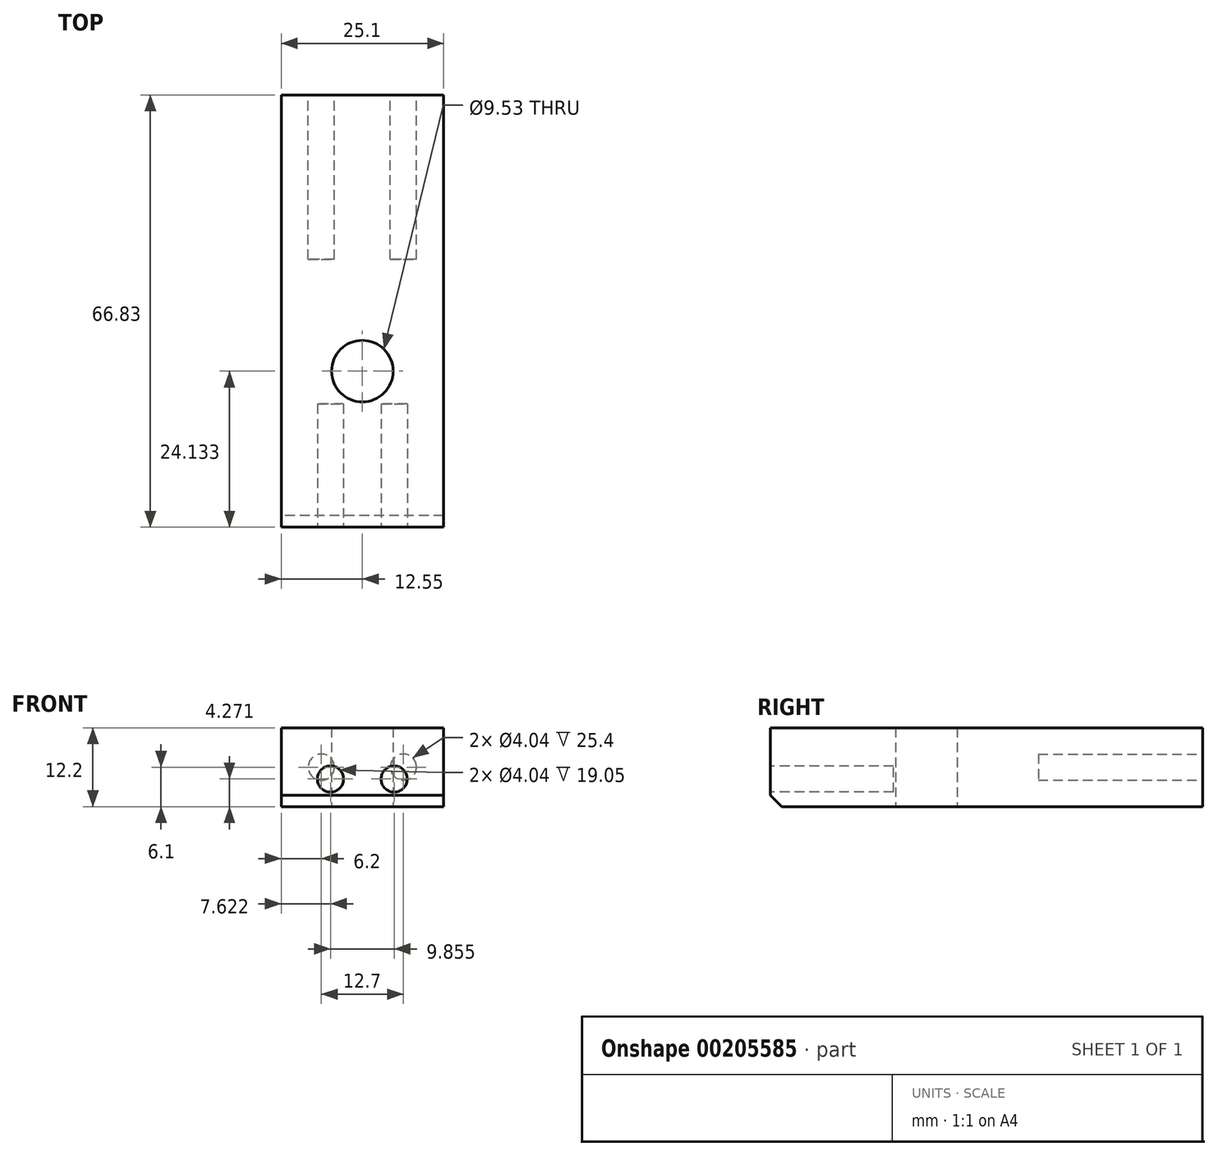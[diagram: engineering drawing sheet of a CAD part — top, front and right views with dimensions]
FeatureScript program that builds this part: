
annotation { "Feature Type Name" : "Feature", "Feature Type Description" : "" }
export const myFeature = defineFeature(function(context is Context, id is Id, definition is map)
    precondition{}
    {
        {
            var Q0;
            Q0=qCreatedBy(makeId("Front.planeOp"),FACE);
            var sketch = newSketch(context, id + "F0", { "sketchPlane" : qUnion([Q0])});
            skLineSegment(sketch, "E0.bottom", {"start": v(-12.55, 6.1) * mm, "end": v(12.55, 6.1) * mm});
            skLineSegment(sketch, "E0.top", {"start": v(-12.55, -6.1) * mm, "end": v(12.55, -6.1) * mm});
            skLineSegment(sketch, "E0.left", {"start": v(-12.55, 6.1) * mm, "end": v(-12.55, -6.1) * mm});
            skLineSegment(sketch, "E0.right", {"start": v(12.55, 6.1) * mm, "end": v(12.55, -6.1) * mm});
            skPoint(sketch, "E0.middle", {"position": v(0, 0) * mm});
            skSolve(sketch);
        }
        {
            var Q0;
            Q0=qSketchRegion(id+"F0",true);
            extrude(context, id + "F1", {"entities" : qUnion([Q0]), "depth" : 66.83 * mm});
        }
        {
            var Q0;
            Q0=makeQuery(id+"F1.opExtrude","CAP_FACE",FACE,{"disambiguationData":[OSD([sQuery(id+"F0.wireOp",EDGE,"E0.bottom"),sQuery(id+"F0.wireOp",EDGE,"E0.top"),sQuery(id+"F0.wireOp",EDGE,"E0.left"),sQuery(id+"F0.wireOp",EDGE,"E0.right")])],"isStart":true});
            var sketch = newSketch(context, id + "F2", { "sketchPlane" : qUnion([Q0])});
            skCircle(sketch, "E1", {"center": v(6.35, 0) * mm, "radius": 2.02 * mm});
            skCircle(sketch, "E2", {"center": v(-6.35, 0) * mm, "radius": 2.02 * mm});
            skSolve(sketch);
        }
        {
            var Q0;
            Q0=qSketchRegion(id+"F2",true);
            extrude(context, id + "F3", {"entities" : qUnion([Q0]), "operationType" : NewBodyOperationType.REMOVE, "oppositeDirection" : true, "depth" : 25.4 * mm});
        }
        {
            var Q0;
            Q0=makeQuery(id+"F1.opExtrude","CAP_FACE",FACE,{"disambiguationData":[OSD([sQuery(id+"F0.wireOp",EDGE,"E0.bottom"),sQuery(id+"F0.wireOp",EDGE,"E0.top"),sQuery(id+"F0.wireOp",EDGE,"E0.left"),sQuery(id+"F0.wireOp",EDGE,"E0.right")])],"isStart":false});
            var sketch = newSketch(context, id + "F4", { "sketchPlane" : qUnion([Q0])});
            skCircle(sketch, "E3", {"center": v(-4.93, -1.83) * mm, "radius": 2.02 * mm});
            skCircle(sketch, "E4", {"center": v(4.93, -1.83) * mm, "radius": 2.02 * mm});
            skSolve(sketch);
        }
        {
            var Q0;
            Q0=qSketchRegion(id+"F4",true);
            extrude(context, id + "F5", {"entities" : qUnion([Q0]), "operationType" : NewBodyOperationType.REMOVE, "oppositeDirection" : true, "depth" : 19.05 * mm});
        }
        {
            var Q0;
            Q0=makeQuery(id+"F1.opExtrude","CAP_EDGE",EDGE,{"disambiguationData":[OSD([sQuery(id+"F0.wireOp",EDGE,"E0.top")])],"isStart":false});
            chamfer(context, id + "F6", {"entities" : qUnion([Q0]), "width" : 1.78 * mm, "tangentPropagation" : true});
        }
        {
            var Q0;
            Q0=makeQuery(id+"F1.opExtrude","SWEPT_FACE",FACE,{"disambiguationData":[OSD([sQuery(id+"F0.wireOp",EDGE,"E0.top")])]});
            var sketch = newSketch(context, id + "F7", { "sketchPlane" : qUnion([Q0])});
            skCircle(sketch, "E5", {"center": v(0, 42.7) * mm, "radius": 4.76 * mm});
            skSolve(sketch);
        }
        {
            var Q0;
            Q0=qSketchRegion(id+"F7",true);
            extrude(context, id + "F8", {"entities" : qUnion([Q0]), "operationType" : NewBodyOperationType.REMOVE, "endBound" : BoundingType.THROUGH_ALL, "oppositeDirection" : true, "depth" : 25.4 * mm});
        }
    });
